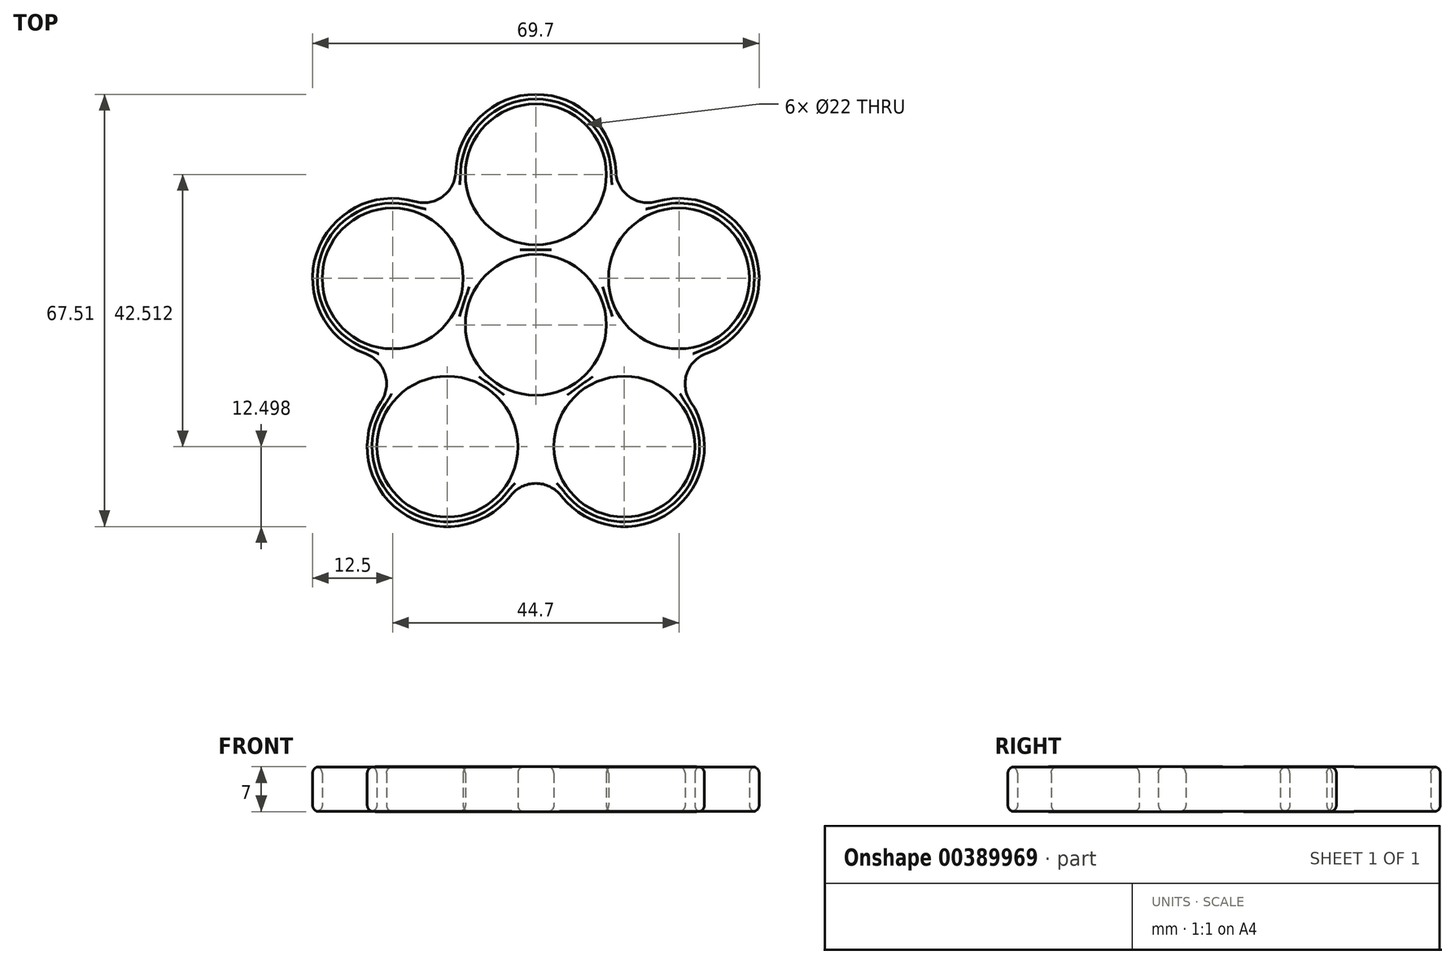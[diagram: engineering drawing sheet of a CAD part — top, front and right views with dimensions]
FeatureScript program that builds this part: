
annotation { "Feature Type Name" : "Feature", "Feature Type Description" : "" }
export const myFeature = defineFeature(function(context is Context, id is Id, definition is map)
    precondition{}
    {
        {
            var Q0;
            Q0=qCreatedBy(makeId("Top.planeOp"),FACE);
            var sketch = newSketch(context, id + "F0", { "sketchPlane" : qUnion([Q0])});
            skCircle(sketch, "E0", {"center": v(0, 0) * mm, "radius": 11 * mm});
            skLineSegment(sketch, "E1", {"start": v(0, 0) * mm, "end": v(0, 23.5) * mm, "construction": true});
            skLineSegment(sketch, "E2", {"start": v(0, 0) * mm, "end": v(22.35, 7.26) * mm, "construction": true});
            skLineSegment(sketch, "E3", {"start": v(0, 0) * mm, "end": v(13.81, -19.01) * mm, "construction": true});
            skLineSegment(sketch, "E4", {"start": v(0, 0) * mm, "end": v(-22.35, 7.26) * mm, "construction": true});
            skLineSegment(sketch, "E5", {"start": v(0, 0) * mm, "end": v(-13.81, -19.01) * mm, "construction": true});
            skCircle(sketch, "E6", {"center": v(0, 23.5) * mm, "radius": 11 * mm});
            skCircle(sketch, "E7", {"center": v(-22.35, 7.26) * mm, "radius": 11 * mm});
            skCircle(sketch, "E8", {"center": v(-13.81, -19.01) * mm, "radius": 11 * mm});
            skCircle(sketch, "E9", {"center": v(13.81, -19.01) * mm, "radius": 11 * mm});
            skCircle(sketch, "E10", {"center": v(22.35, 7.26) * mm, "radius": 11 * mm});
            skArc(sketch, "E11", {"start": v(12.5, 23.9) * mm, "mid": v(0, 36) * mm, "end": v(-12.5, 23.9) * mm});
            skArc(sketch, "E12", {"start": v(-18.88, 19.27) * mm, "mid": v(-34.24, 11.12) * mm, "end": v(-26.6, -4.5) * mm});
            skArc(sketch, "E13", {"start": v(-24.16, -12) * mm, "mid": v(-21.16, -29.12) * mm, "end": v(-3.95, -26.69) * mm});
            skArc(sketch, "E14", {"start": v(3.95, -26.69) * mm, "mid": v(21.16, -29.12) * mm, "end": v(24.16, -12) * mm});
            skArc(sketch, "E15", {"start": v(26.6, -4.5) * mm, "mid": v(34.24, 11.12) * mm, "end": v(18.88, 19.27) * mm});
            skArc(sketch, "E16", {"start": v(-18.88, 19.27) * mm, "mid": v(-14.55, 20.03) * mm, "end": v(-12.5, 23.9) * mm});
            skArc(sketch, "E17", {"start": v(-24.16, -12) * mm, "mid": v(-23.55, -7.65) * mm, "end": v(-26.6, -4.5) * mm});
            skArc(sketch, "E18", {"start": v(3.95, -26.69) * mm, "mid": v(0, -24.76) * mm, "end": v(-3.95, -26.69) * mm});
            skArc(sketch, "E19", {"start": v(12.5, 23.9) * mm, "mid": v(14.55, 20.03) * mm, "end": v(18.88, 19.27) * mm});
            skArc(sketch, "E20", {"start": v(26.6, -4.5) * mm, "mid": v(23.55, -7.65) * mm, "end": v(24.16, -12) * mm});
            skSolve(sketch);
        }
        {
            var Q0;
            Q0=makeQuery(id+"F0.imprint","IMPRINT",FACE,{"disambiguationData":[TD([[makeQuery(id+"F0.imprint","IMPRINT",EDGE,{"derivedFrom":sQuery(id+"F0.wireOp",EDGE,"E0")}),-1.0]])]});
            extrude(context, id + "F1", {"entities" : qUnion([Q0]), "depth" : 7 * mm});
        }
        {
            var Q0;
            Q0=makeQuery(id+"F1.opExtrude","CAP_EDGE",EDGE,{"disambiguationData":[OSD([sQuery(id+"F0.wireOp",EDGE,"E12")])],"isStart":false});
            var Q1;
            Q1=makeQuery(id+"F1.opExtrude","CAP_EDGE",EDGE,{"disambiguationData":[OSD([sQuery(id+"F0.wireOp",EDGE,"E13")])],"isStart":true});
            var Q2;
            Q2=makeQuery(id+"F1.opExtrude","CAP_EDGE",EDGE,{"disambiguationData":[OSD([sQuery(id+"F0.wireOp",EDGE,"E8")])],"isStart":false});
            var Q3;
            Q3=makeQuery(id+"F1.opExtrude","CAP_EDGE",EDGE,{"disambiguationData":[OSD([sQuery(id+"F0.wireOp",EDGE,"E7")])],"isStart":false});
            var Q4;
            Q4=makeQuery(id+"F1.opExtrude","CAP_EDGE",EDGE,{"disambiguationData":[OSD([sQuery(id+"F0.wireOp",EDGE,"E6")])],"isStart":true});
            var Q5;
            Q5=makeQuery(id+"F1.opExtrude","CAP_EDGE",EDGE,{"disambiguationData":[OSD([sQuery(id+"F0.wireOp",EDGE,"E6")])],"isStart":false});
            var Q6;
            Q6=makeQuery(id+"F1.opExtrude","CAP_EDGE",EDGE,{"disambiguationData":[OSD([sQuery(id+"F0.wireOp",EDGE,"E7")])],"isStart":true});
            var Q7;
            Q7=makeQuery(id+"F1.opExtrude","CAP_EDGE",EDGE,{"disambiguationData":[OSD([sQuery(id+"F0.wireOp",EDGE,"E8")])],"isStart":true});
            var Q8;
            Q8=makeQuery(id+"F1.opExtrude","CAP_EDGE",EDGE,{"disambiguationData":[OSD([sQuery(id+"F0.wireOp",EDGE,"E0")])],"isStart":true});
            var Q9;
            Q9=makeQuery(id+"F1.opExtrude","CAP_EDGE",EDGE,{"disambiguationData":[OSD([sQuery(id+"F0.wireOp",EDGE,"E0")])],"isStart":false});
            var Q10;
            Q10=makeQuery(id+"F1.opExtrude","CAP_EDGE",EDGE,{"disambiguationData":[OSD([sQuery(id+"F0.wireOp",EDGE,"E10")])],"isStart":true});
            var Q11;
            Q11=makeQuery(id+"F1.opExtrude","CAP_EDGE",EDGE,{"disambiguationData":[OSD([sQuery(id+"F0.wireOp",EDGE,"E10")])],"isStart":false});
            var Q12;
            Q12=makeQuery(id+"F1.opExtrude","CAP_EDGE",EDGE,{"disambiguationData":[OSD([sQuery(id+"F0.wireOp",EDGE,"E9")])],"isStart":true});
            var Q13;
            Q13=makeQuery(id+"F1.opExtrude","CAP_EDGE",EDGE,{"disambiguationData":[OSD([sQuery(id+"F0.wireOp",EDGE,"E9")])],"isStart":false});
            fillet(context, id + "F2", {"entities" : qUnion([Q0, Q1, Q2, Q3, Q4, Q5, Q6, Q7, Q8, Q9, Q10, Q11, Q12, Q13]), "radius" : 1 * mm, "tangentPropagation" : true, "allowEdgeOverflow" : false});
        }
    });
